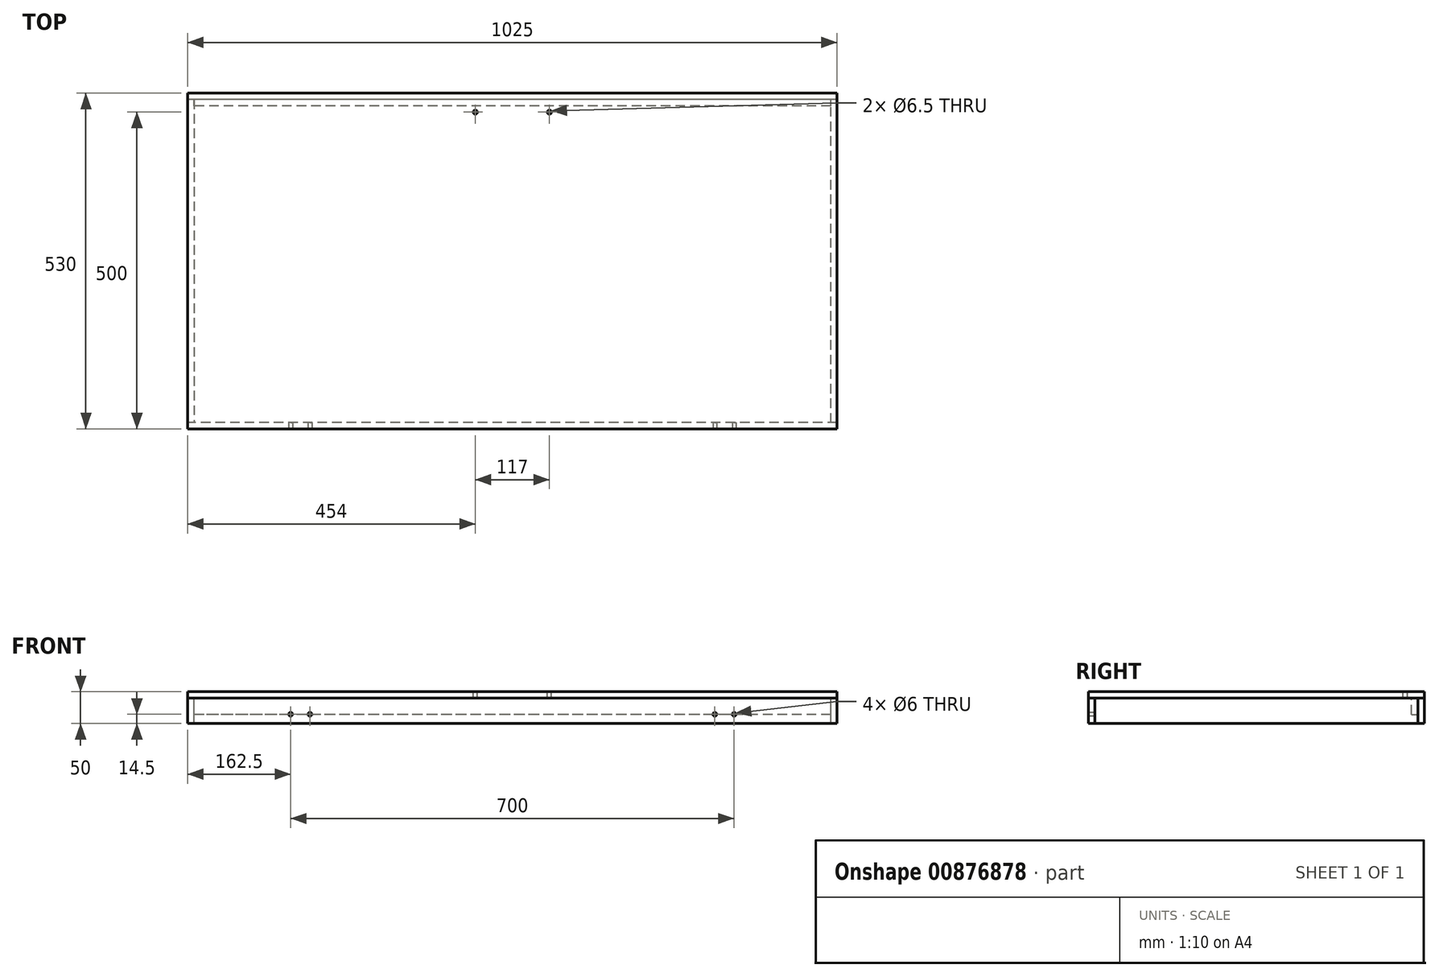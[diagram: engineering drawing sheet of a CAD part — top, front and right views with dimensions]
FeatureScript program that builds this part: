
annotation { "Feature Type Name" : "Feature", "Feature Type Description" : "" }
export const myFeature = defineFeature(function(context is Context, id is Id, definition is map)
    precondition{}
    {
        {
            var Q0;
            Q0=qCreatedBy(makeId("Top.planeOp"),FACE);
            var sketch = newSketch(context, id + "F0", { "sketchPlane" : qUnion([Q0])});
            skLineSegment(sketch, "E0.bottom", {"start": v(512.5, 265) * mm, "end": v(-512.5, 265) * mm});
            skLineSegment(sketch, "E0.top", {"start": v(512.5, -265) * mm, "end": v(-512.5, -265) * mm});
            skLineSegment(sketch, "E0.left", {"start": v(512.5, 265) * mm, "end": v(512.5, -265) * mm});
            skLineSegment(sketch, "E0.right", {"start": v(-512.5, 265) * mm, "end": v(-512.5, -265) * mm});
            skPoint(sketch, "E0.middle", {"position": v(0, 0) * mm});
            skSolve(sketch);
        }
        {
            var Q0;
            Q0=makeQuery(id+"F0.imprint","IMPRINT",FACE,{"disambiguationData":[TD([[makeQuery(id+"F0.imprint","IMPRINT",EDGE,{"derivedFrom":sQuery(id+"F0.wireOp",EDGE,"E0.bottom")}),1.0]])]});
            extrude(context, id + "F1", {"entities" : qUnion([Q0]), "depth" : 10 * mm, "offsetDistance" : 25 * mm});
        }
        {
            var Q0;
            Q0=makeQuery(id+"F1.opExtrude","CAP_FACE",FACE,{"disambiguationData":[OSD([sQuery(id+"F0.wireOp",EDGE,"E0.bottom"),sQuery(id+"F0.wireOp",EDGE,"E0.top"),sQuery(id+"F0.wireOp",EDGE,"E0.left"),sQuery(id+"F0.wireOp",EDGE,"E0.right")])],"isStart":true});
            var sketch = newSketch(context, id + "F2", { "sketchPlane" : qUnion([Q0])});
            skLineSegment(sketch, "E1.bottom", {"start": v(512.5, 255) * mm, "end": v(-512.5, 255) * mm});
            skLineSegment(sketch, "E1.top", {"start": v(512.5, 265) * mm, "end": v(-512.5, 265) * mm});
            skLineSegment(sketch, "E1.left", {"start": v(512.5, 255) * mm, "end": v(512.5, 265) * mm});
            skLineSegment(sketch, "E1.right", {"start": v(-512.5, 255) * mm, "end": v(-512.5, 265) * mm});
            skPoint(sketch, "E1.middle", {"position": v(0, 260) * mm});
            skSolve(sketch);
        }
        {
            var Q0;
            Q0=makeQuery(id+"F2.imprint","IMPRINT",FACE,{"disambiguationData":[TD([[makeQuery(id+"F2.imprint","IMPRINT",EDGE,{"derivedFrom":sQuery(id+"F2.wireOp",EDGE,"E1.bottom")}),-1.0]])]});
            extrude(context, id + "F3", {"entities" : qUnion([Q0]), "depth" : 40 * mm, "offsetDistance" : 25 * mm});
        }
        {
            var Q0;
            Q0=makeQuery(id+"F3.opExtrude","SWEPT_BODY",BODY,{"disambiguationData":[OSD([sQuery(id+"F2.wireOp",EDGE,"E1.bottom"),sQuery(id+"F2.wireOp",EDGE,"E1.top"),sQuery(id+"F2.wireOp",EDGE,"E1.left"),sQuery(id+"F2.wireOp",EDGE,"E1.right")])]});
            transform(context, id + "F4", {"entities" : qUnion([Q0]), "transformType" : TransformType.TRANSLATION_3D, "dx" : 0 * mm, "dy" : 520 * mm, "dz" : 0 * mm, "makeCopy" : true});
        }
        {
            var Q0;
            Q0=makeQuery(id+"F1.opExtrude","CAP_FACE",FACE,{"disambiguationData":[OSD([sQuery(id+"F0.wireOp",EDGE,"E0.bottom"),sQuery(id+"F0.wireOp",EDGE,"E0.top"),sQuery(id+"F0.wireOp",EDGE,"E0.left"),sQuery(id+"F0.wireOp",EDGE,"E0.right")])],"isStart":true});
            var sketch = newSketch(context, id + "F5", { "sketchPlane" : qUnion([Q0])});
            skLineSegment(sketch, "E2.bottom", {"start": v(512.5, 255) * mm, "end": v(502.5, 255) * mm});
            skLineSegment(sketch, "E2.top", {"start": v(512.5, -255) * mm, "end": v(502.5, -255) * mm});
            skLineSegment(sketch, "E2.left", {"start": v(512.5, 255) * mm, "end": v(512.5, -255) * mm});
            skLineSegment(sketch, "E2.right", {"start": v(502.5, 255) * mm, "end": v(502.5, -255) * mm});
            skPoint(sketch, "E2.middle", {"position": v(507.5, 0) * mm});
            skSolve(sketch);
        }
        {
            var Q0;
            Q0=makeQuery(id+"F5.imprint","IMPRINT",FACE,{"disambiguationData":[TD([[makeQuery(id+"F5.imprint","IMPRINT",EDGE,{"derivedFrom":sQuery(id+"F5.wireOp",EDGE,"E2.bottom")}),1.0]])]});
            extrude(context, id + "F6", {"entities" : qUnion([Q0]), "depth" : 40 * mm, "offsetDistance" : 25 * mm});
        }
        {
            var Q0;
            Q0=makeQuery(id+"F6.opExtrude","SWEPT_BODY",BODY,{"disambiguationData":[OSD([sQuery(id+"F5.wireOp",EDGE,"E2.bottom"),sQuery(id+"F5.wireOp",EDGE,"E2.top"),sQuery(id+"F5.wireOp",EDGE,"E2.left"),sQuery(id+"F5.wireOp",EDGE,"E2.right")])]});
            transform(context, id + "F7", {"entities" : qUnion([Q0]), "transformType" : TransformType.TRANSLATION_3D, "dx" : -1015 * mm, "dy" : 0 * mm, "dz" : 0 * mm, "makeCopy" : true});
        }
        {
            var Q0;
            Q0=makeQuery(id+"F3.opExtrude","SWEPT_FACE",FACE,{"disambiguationData":[OSD([sQuery(id+"F2.wireOp",EDGE,"E1.top")])]});
            var sketch = newSketch(context, id + "F8", { "sketchPlane" : qUnion([Q0])});
            skPoint(sketch, "E3", {"position": v(-350, -25.5) * mm});
            skPoint(sketch, "E4", {"position": v(-319.5, -25.5) * mm});
            skPoint(sketch, "E5", {"position": v(319.5, -25.5) * mm});
            skPoint(sketch, "E6", {"position": v(350, -25.5) * mm});
            skSolve(sketch);
        }
        {
            var Q0;
            Q0=sQuery(id+"F8.wireOp",VERTEX,"E3");
            var Q1;
            Q1=sQuery(id+"F8.wireOp",VERTEX,"E4");
            var Q2;
            Q2=sQuery(id+"F8.wireOp",VERTEX,"E5");
            var Q3;
            Q3=sQuery(id+"F8.wireOp",VERTEX,"E6");
            var Q4;
            Q4=makeQuery(id+"F3.opExtrude","SWEPT_BODY",BODY,{"disambiguationData":[OSD([sQuery(id+"F2.wireOp",EDGE,"E1.bottom"),sQuery(id+"F2.wireOp",EDGE,"E1.top"),sQuery(id+"F2.wireOp",EDGE,"E1.left"),sQuery(id+"F2.wireOp",EDGE,"E1.right")])]});
            hole(context, id + "F9", {"style" : HoleStyle.SIMPLE, "endStyle" : HoleEndStyle.BLIND, "holeDiameter" : 6 * mm, "majorDiameter" : 5 * mm, "holeDepth" : 15 * mm, "isTappedThrough" : true, "tappedDepth" : 12 * mm, "tapClearance" : 3, "locations" : qUnion([Q0, Q1, Q2, Q3]), "scope" : qUnion([Q4])});
        }
        {
            var Q0;
            Q0=makeQuery(id+"F1.opExtrude","CAP_FACE",FACE,{"disambiguationData":[OSD([sQuery(id+"F0.wireOp",EDGE,"E0.bottom"),sQuery(id+"F0.wireOp",EDGE,"E0.top"),sQuery(id+"F0.wireOp",EDGE,"E0.left"),sQuery(id+"F0.wireOp",EDGE,"E0.right")])],"isStart":true});
            var sketch = newSketch(context, id + "F10", { "sketchPlane" : qUnion([Q0])});
            skLineSegment(sketch, "E7.bottom", {"start": v(502.5, -245) * mm, "end": v(-502.5, -245) * mm});
            skLineSegment(sketch, "E7.top", {"start": v(502.5, -255) * mm, "end": v(-502.5, -255) * mm});
            skLineSegment(sketch, "E7.left", {"start": v(502.5, -245) * mm, "end": v(502.5, -255) * mm});
            skLineSegment(sketch, "E7.right", {"start": v(-502.5, -245) * mm, "end": v(-502.5, -255) * mm});
            skPoint(sketch, "E7.middle", {"position": v(0, -250) * mm});
            skSolve(sketch);
        }
        {
            var Q0;
            Q0=makeQuery(id+"F10.imprint","IMPRINT",FACE,{"disambiguationData":[TD([[makeQuery(id+"F10.imprint","IMPRINT",EDGE,{"derivedFrom":sQuery(id+"F10.wireOp",EDGE,"E7.bottom")}),1.0]])]});
            extrude(context, id + "F11", {"entities" : qUnion([Q0]), "depth" : 26 * mm, "offsetDistance" : 25 * mm});
        }
        {
            var Q0;
            Q0=makeQuery(id+"F1.opExtrude","CAP_FACE",FACE,{"disambiguationData":[OSD([sQuery(id+"F0.wireOp",EDGE,"E0.bottom"),sQuery(id+"F0.wireOp",EDGE,"E0.top"),sQuery(id+"F0.wireOp",EDGE,"E0.left"),sQuery(id+"F0.wireOp",EDGE,"E0.right")])],"isStart":false});
            var sketch = newSketch(context, id + "F12", { "sketchPlane" : qUnion([Q0])});
            skPoint(sketch, "E8", {"position": v(58.5, 235) * mm});
            skPoint(sketch, "E9", {"position": v(-58.5, 235) * mm});
            skLineSegment(sketch, "E10", {"start": v(-58.5, 235) * mm, "end": v(58.5, 235) * mm});
            skLineSegment(sketch, "E11", {"start": v(0, 0) * mm, "end": v(0, 235) * mm});
            skSolve(sketch);
        }
        {
            var Q0;
            Q0=sQuery(id+"F12.wireOp",VERTEX,"E9");
            var Q1;
            Q1=sQuery(id+"F12.wireOp",VERTEX,"E8");
            var Q2;
            Q2=makeQuery(id+"F1.opExtrude","SWEPT_BODY",BODY,{"disambiguationData":[OSD([sQuery(id+"F0.wireOp",EDGE,"E0.bottom"),sQuery(id+"F0.wireOp",EDGE,"E0.top"),sQuery(id+"F0.wireOp",EDGE,"E0.left"),sQuery(id+"F0.wireOp",EDGE,"E0.right")])]});
            hole(context, id + "F13", {"style" : HoleStyle.SIMPLE, "endStyle" : HoleEndStyle.BLIND, "holeDiameter" : 6.5 * mm, "majorDiameter" : 5 * mm, "holeDepth" : 15 * mm, "isTappedThrough" : true, "tappedDepth" : 12 * mm, "tapClearance" : 3, "locations" : qUnion([Q0, Q1]), "scope" : qUnion([Q2])});
        }
    });
